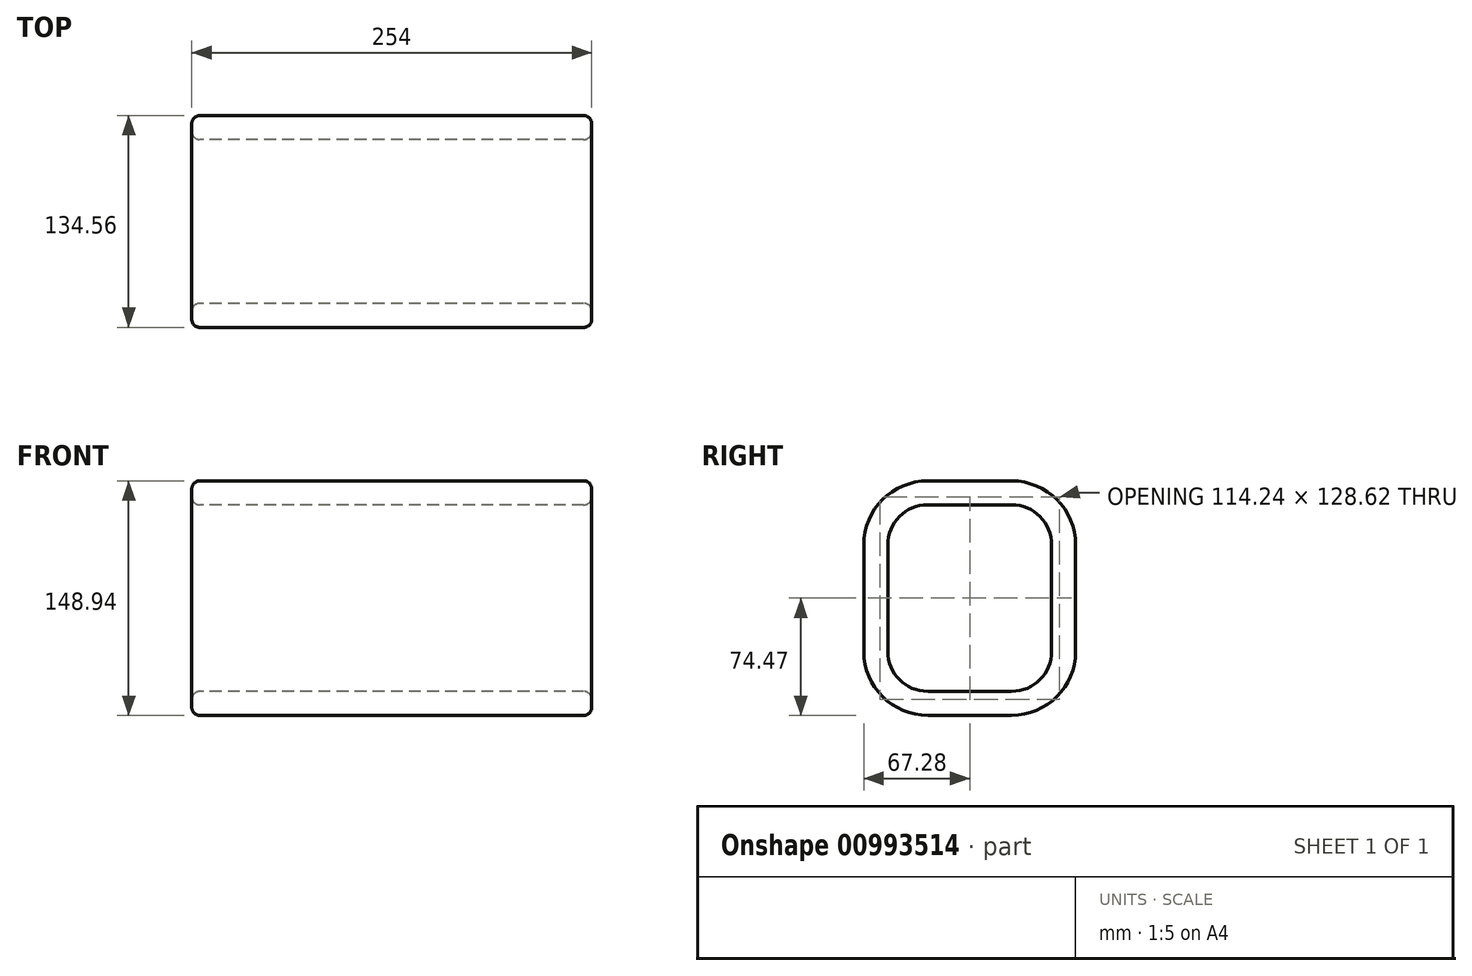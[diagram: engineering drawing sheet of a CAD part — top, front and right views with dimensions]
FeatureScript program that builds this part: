
annotation { "Feature Type Name" : "Feature", "Feature Type Description" : "" }
export const myFeature = defineFeature(function(context is Context, id is Id, definition is map)
    precondition{}
    {
        {
            var Q0;
            Q0=qCreatedBy(makeId("Right.planeOp"),FACE);
            var sketch = newSketch(context, id + "F0", { "sketchPlane" : qUnion([Q0])});
            skLineSegment(sketch, "E0.bottom", {"start": v(-21.52, 61.66) * mm, "end": v(31.76, 61.66) * mm});
            skLineSegment(sketch, "E0.top", {"start": v(-21.52, -56.8) * mm, "end": v(31.76, -56.8) * mm});
            skLineSegment(sketch, "E0.left", {"start": v(-46.92, 36.26) * mm, "end": v(-46.92, -31.4) * mm});
            skLineSegment(sketch, "E0.right", {"start": v(57.16, 36.26) * mm, "end": v(57.16, -31.4) * mm});
            skPoint(sketch, "E1.visualSharp", {"position": v(-46.92, 61.66) * mm});
            skArc(sketch, "E1.filletArc", {"start": v(-21.52, 61.66) * mm, "mid": v(-39.48, 54.22) * mm, "end": v(-46.92, 36.26) * mm});
            skPoint(sketch, "E2.visualSharp", {"position": v(57.16, 61.66) * mm});
            skArc(sketch, "E2.filletArc", {"start": v(57.16, 36.26) * mm, "mid": v(49.72, 54.22) * mm, "end": v(31.76, 61.66) * mm});
            skPoint(sketch, "E3.visualSharp", {"position": v(-46.92, -56.8) * mm});
            skArc(sketch, "E3.filletArc", {"start": v(-46.92, -31.4) * mm, "mid": v(-39.48, -49.36) * mm, "end": v(-21.52, -56.8) * mm});
            skPoint(sketch, "E4.visualSharp", {"position": v(57.16, -56.8) * mm});
            skArc(sketch, "E4.filletArc", {"start": v(31.76, -56.8) * mm, "mid": v(49.72, -49.36) * mm, "end": v(57.16, -31.4) * mm});
            skArc(sketch, "E5.0", {"start": v(72.4, 36.26) * mm, "mid": v(60.5, 65) * mm, "end": v(31.76, 76.9) * mm});
            skLineSegment(sketch, "E5.1", {"start": v(-21.52, 76.9) * mm, "end": v(31.76, 76.9) * mm});
            skLineSegment(sketch, "E5.2", {"start": v(72.4, 36.26) * mm, "end": v(72.4, -31.4) * mm});
            skArc(sketch, "E5.3", {"start": v(-21.52, 76.9) * mm, "mid": v(-50.26, 65) * mm, "end": v(-62.16, 36.26) * mm});
            skArc(sketch, "E5.4", {"start": v(31.76, -72.04) * mm, "mid": v(60.5, -60.14) * mm, "end": v(72.4, -31.4) * mm});
            skLineSegment(sketch, "E5.5", {"start": v(-21.52, -72.04) * mm, "end": v(31.76, -72.04) * mm});
            skArc(sketch, "E5.6", {"start": v(-62.16, -31.4) * mm, "mid": v(-50.26, -60.14) * mm, "end": v(-21.52, -72.04) * mm});
            skLineSegment(sketch, "E5.7", {"start": v(-62.16, 36.26) * mm, "end": v(-62.16, -31.4) * mm});
            skSolve(sketch);
        }
        {
            var Q0;
            Q0 = qSketchRegion(id + "F0", true);
            extrude(context, id + "F1", {"entities" : qUnion([Q0]), "depth" : 254 * mm, "offsetDistance" : 25.4 * mm});
        }
        {
            var Q0;
            Q0=makeQuery(id+"F1.opExtrude","CAP_EDGE",EDGE,{"disambiguationData":[OSD([sQuery(id+"F0.wireOp",EDGE,"E0.bottom")])],"isStart":false});
            var Q1;
            Q1=makeQuery(id+"F1.opExtrude","CAP_EDGE",EDGE,{"disambiguationData":[OSD([sQuery(id+"F0.wireOp",EDGE,"E5.1")])],"isStart":false});
            var Q2;
            Q2=makeQuery(id+"F1.opExtrude","CAP_EDGE",EDGE,{"disambiguationData":[OSD([sQuery(id+"F0.wireOp",EDGE,"E5.0")])],"isStart":false});
            var Q3;
            Q3=makeQuery(id+"F1.opExtrude","CAP_EDGE",EDGE,{"disambiguationData":[OSD([sQuery(id+"F0.wireOp",EDGE,"E2.filletArc")])],"isStart":false});
            var Q4;
            Q4=makeQuery(id+"F1.opExtrude","CAP_EDGE",EDGE,{"disambiguationData":[OSD([sQuery(id+"F0.wireOp",EDGE,"E0.right")])],"isStart":false});
            var Q5;
            Q5=makeQuery(id+"F1.opExtrude","CAP_EDGE",EDGE,{"disambiguationData":[OSD([sQuery(id+"F0.wireOp",EDGE,"E5.4")])],"isStart":false});
            var Q6;
            Q6=makeQuery(id+"F1.opExtrude","CAP_EDGE",EDGE,{"disambiguationData":[OSD([sQuery(id+"F0.wireOp",EDGE,"E4.filletArc")])],"isStart":false});
            var Q7;
            Q7=makeQuery(id+"F1.opExtrude","CAP_EDGE",EDGE,{"disambiguationData":[OSD([sQuery(id+"F0.wireOp",EDGE,"E5.2")])],"isStart":false});
            var Q8;
            Q8=makeQuery(id+"F1.opExtrude","CAP_EDGE",EDGE,{"disambiguationData":[OSD([sQuery(id+"F0.wireOp",EDGE,"E0.top")])],"isStart":false});
            var Q9;
            Q9=makeQuery(id+"F1.opExtrude","CAP_EDGE",EDGE,{"disambiguationData":[OSD([sQuery(id+"F0.wireOp",EDGE,"E5.5")])],"isStart":false});
            var Q10;
            Q10=makeQuery(id+"F1.opExtrude","CAP_EDGE",EDGE,{"disambiguationData":[OSD([sQuery(id+"F0.wireOp",EDGE,"E3.filletArc")])],"isStart":false});
            var Q11;
            Q11=makeQuery(id+"F1.opExtrude","CAP_EDGE",EDGE,{"disambiguationData":[OSD([sQuery(id+"F0.wireOp",EDGE,"E5.6")])],"isStart":false});
            var Q12;
            Q12=makeQuery(id+"F1.opExtrude","CAP_EDGE",EDGE,{"disambiguationData":[OSD([sQuery(id+"F0.wireOp",EDGE,"E5.7")])],"isStart":false});
            var Q13;
            Q13=makeQuery(id+"F1.opExtrude","CAP_EDGE",EDGE,{"disambiguationData":[OSD([sQuery(id+"F0.wireOp",EDGE,"E0.left")])],"isStart":false});
            var Q14;
            Q14=makeQuery(id+"F1.opExtrude","CAP_EDGE",EDGE,{"disambiguationData":[OSD([sQuery(id+"F0.wireOp",EDGE,"E5.3")])],"isStart":false});
            var Q15;
            Q15=makeQuery(id+"F1.opExtrude","CAP_EDGE",EDGE,{"disambiguationData":[OSD([sQuery(id+"F0.wireOp",EDGE,"E1.filletArc")])],"isStart":false});
            var Q16;
            Q16=makeQuery(id+"F1.opExtrude","CAP_EDGE",EDGE,{"disambiguationData":[OSD([sQuery(id+"F0.wireOp",EDGE,"E5.2")])],"isStart":true});
            var Q17;
            Q17=makeQuery(id+"F1.opExtrude","CAP_EDGE",EDGE,{"disambiguationData":[OSD([sQuery(id+"F0.wireOp",EDGE,"E0.right")])],"isStart":true});
            var Q18;
            Q18=makeQuery(id+"F1.opExtrude","CAP_EDGE",EDGE,{"disambiguationData":[OSD([sQuery(id+"F0.wireOp",EDGE,"E5.0")])],"isStart":true});
            var Q19;
            Q19=makeQuery(id+"F1.opExtrude","CAP_EDGE",EDGE,{"disambiguationData":[OSD([sQuery(id+"F0.wireOp",EDGE,"E0.bottom")])],"isStart":true});
            var Q20;
            Q20=makeQuery(id+"F1.opExtrude","CAP_EDGE",EDGE,{"disambiguationData":[OSD([sQuery(id+"F0.wireOp",EDGE,"E2.filletArc")])],"isStart":true});
            var Q21;
            Q21=makeQuery(id+"F1.opExtrude","CAP_EDGE",EDGE,{"disambiguationData":[OSD([sQuery(id+"F0.wireOp",EDGE,"E5.1")])],"isStart":true});
            var Q22;
            Q22=makeQuery(id+"F1.opExtrude","CAP_EDGE",EDGE,{"disambiguationData":[OSD([sQuery(id+"F0.wireOp",EDGE,"E5.3")])],"isStart":true});
            var Q23;
            Q23=makeQuery(id+"F1.opExtrude","CAP_EDGE",EDGE,{"disambiguationData":[OSD([sQuery(id+"F0.wireOp",EDGE,"E1.filletArc")])],"isStart":true});
            var Q24;
            Q24=makeQuery(id+"F1.opExtrude","CAP_EDGE",EDGE,{"disambiguationData":[OSD([sQuery(id+"F0.wireOp",EDGE,"E0.left")])],"isStart":true});
            var Q25;
            Q25=makeQuery(id+"F1.opExtrude","CAP_EDGE",EDGE,{"disambiguationData":[OSD([sQuery(id+"F0.wireOp",EDGE,"E5.7")])],"isStart":true});
            var Q26;
            Q26=makeQuery(id+"F1.opExtrude","CAP_EDGE",EDGE,{"disambiguationData":[OSD([sQuery(id+"F0.wireOp",EDGE,"E5.6")])],"isStart":true});
            var Q27;
            Q27=makeQuery(id+"F1.opExtrude","CAP_EDGE",EDGE,{"disambiguationData":[OSD([sQuery(id+"F0.wireOp",EDGE,"E3.filletArc")])],"isStart":true});
            var Q28;
            Q28=makeQuery(id+"F1.opExtrude","CAP_EDGE",EDGE,{"disambiguationData":[OSD([sQuery(id+"F0.wireOp",EDGE,"E5.5")])],"isStart":true});
            var Q29;
            Q29=makeQuery(id+"F1.opExtrude","CAP_EDGE",EDGE,{"disambiguationData":[OSD([sQuery(id+"F0.wireOp",EDGE,"E0.top")])],"isStart":true});
            var Q30;
            Q30=makeQuery(id+"F1.opExtrude","CAP_EDGE",EDGE,{"disambiguationData":[OSD([sQuery(id+"F0.wireOp",EDGE,"E5.4")])],"isStart":true});
            var Q31;
            Q31=makeQuery(id+"F1.opExtrude","CAP_EDGE",EDGE,{"disambiguationData":[OSD([sQuery(id+"F0.wireOp",EDGE,"E4.filletArc")])],"isStart":true});
            fillet(context, id + "F2", {"entities" : qUnion([Q0, Q1, Q2, Q3, Q4, Q5, Q6, Q7, Q8, Q9, Q10, Q11, Q12, Q13, Q14, Q15, Q16, Q17, Q18, Q19, Q20, Q21, Q22, Q23, Q24, Q25, Q26, Q27, Q28, Q29, Q30, Q31]), "radius" : 5.08 * mm, "tangentPropagation" : true, "allowEdgeOverflow" : false});
        }
    });
